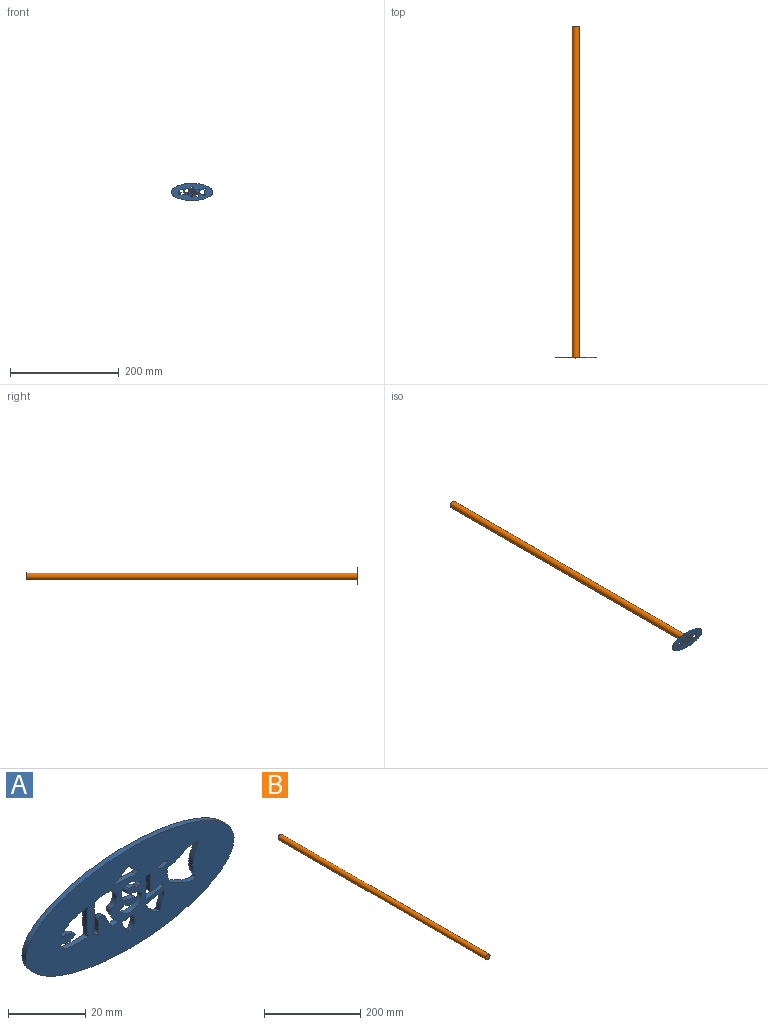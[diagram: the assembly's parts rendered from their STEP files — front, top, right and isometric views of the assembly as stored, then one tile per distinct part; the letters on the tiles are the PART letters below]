
ASSEMBLY  parts=2 mates=1
PART A: 74 faces, bbox 76.2x1.6x31.8 mm
  f0: plane 76.2x31.75mm, normal (0,-1,0), area 1556.4mm2, adj f2,f3,f4,f5,f6,f7,f8,f9
  f1: plane 76.2x31.75mm, normal (0,1,0), area 1556.4mm2, adj f2,f3,f4,f5,f6,f7,f8,f9
  f2: extruded ~76.2x31.75mm, area 280.8mm2, adj f0,f1
  f3: cylinder r=18.2mm len=1.77mm, axis (0,-1,0), area 2.9mm2, adj f0,f1,f4,f9
  f4: cylinder r=740.75mm len=7.68mm, axis (0,-1,0), area 12.2mm2, adj f0,f1,f3,f5
  f5: cylinder r=37.19mm len=6.75mm, axis (0,-1,0), area 10.9mm2, adj f0,f1,f4,f6
  f6: cylinder r=4.49mm len=1.59mm, axis (0,-1,0), area 1.1mm2, adj f0,f1,f5,f7
  f7: cylinder r=0.59mm len=1.59mm, axis (0,-1,0), area 1.5mm2, adj f0,f1,f6,f8
  f8: cylinder r=127.81mm len=3.97mm, axis (0,-1,0), area 6.4mm2, adj f0,f1,f7,f9
  f9: cylinder r=424.89mm len=5.64mm, axis (0,-1,0), area 9mm2, adj f0,f1,f3,f8
  f10: cylinder r=145.51mm len=6.76mm, axis (0,-1,0), area 11mm2, adj f0,f1,f11,f13
  f11: cylinder r=9.14mm len=5.32mm, axis (0,-1,0), area 11.6mm2, adj f0,f1,f10,f12
  f12: cylinder r=9.63mm len=3.56mm, axis (0,-1,0), area 6mm2, adj f0,f1,f11,f13
  f13: cylinder r=3.4mm len=2.63mm, axis (0,-1,0), area 4.3mm2, adj f0,f1,f10,f12
  f14: cylinder r=0.35mm len=1.59mm, axis (0,-1,0), area 1.1mm2, adj f0,f1,f15,f17
  f15: cylinder r=2.95mm len=3.55mm, axis (0,-1,0), area 6.2mm2, adj f0,f1,f14,f16
  f16: cylinder r=3.58mm len=1.59mm, axis (0,-1,0), area 2.4mm2, adj f0,f1,f15,f17
  f17: cylinder r=16.1mm len=2.17mm, axis (0,-1,0), area 3.6mm2, adj f0,f1,f14,f16
  f18: cylinder r=12.75mm len=5.47mm, axis (0,-1,0), area 9.2mm2, adj f0,f1,f19,f25
  f19: cylinder r=6.86mm len=5.43mm, axis (0,-1,0), area 9.1mm2, adj f0,f1,f18,f20
  f20: cylinder r=41.77mm len=4.82mm, axis (0,-1,0), area 8.4mm2, adj f0,f1,f19,f21
  f21: cylinder r=10.69mm len=4.41mm, axis (0,-1,0), area 7.3mm2, adj f0,f1,f20,f22
  f22: cylinder r=0.46mm len=1.59mm, axis (0,-1,0), area 1.4mm2, adj f0,f1,f21,f23
  f23: cylinder r=7.17mm len=7.4mm, axis (0,-1,0), area 12.4mm2, adj f0,f1,f22,f24
  f24: cylinder r=84.15mm len=3.6mm, axis (0,-1,0), area 6.3mm2, adj f0,f1,f23,f25
  f25: cylinder r=10.84mm len=6.23mm, axis (0,-1,0), area 10.2mm2, adj f0,f1,f18,f24
  f26: cylinder r=117.25mm len=9.33mm, axis (0,-1,0), area 14.8mm2, adj f0,f1,f27,f38
  f27: cylinder r=1.23mm len=1.59mm, axis (0,-1,0), area 2.5mm2, adj f0,f1,f26,f28
  f28: cylinder r=0.52mm len=1.59mm, axis (0,-1,0), area 1.5mm2, adj f0,f1,f27,f29
  f29: cylinder r=29.74mm len=3.77mm, axis (0,-1,0), area 6mm2, adj f0,f1,f28,f30
  f30: cylinder r=0.75mm len=1.59mm, axis (0,-1,0), area 1.7mm2, adj f0,f1,f29,f31
  f31: cylinder r=1.82mm len=1.68mm, axis (0,-1,0), area 3.3mm2, adj f0,f1,f30,f32
  f32: cylinder r=66.39mm len=4.18mm, axis (0,-1,0), area 7.6mm2, adj f0,f1,f31,f33
  f33: cylinder r=5.51mm len=2.03mm, axis (0,-1,0), area 3.4mm2, adj f0,f1,f32,f34
  f34: cylinder r=65.37mm len=4.03mm, axis (0,-1,0), area 7.5mm2, adj f0,f1,f33,f35
  f35: cylinder r=0.86mm len=1.59mm, axis (0,-1,0), area 2.2mm2, adj f0,f1,f34,f36
  f36: cylinder r=3.11mm len=5.81mm, axis (0,-1,0), area 12mm2, adj f0,f1,f35,f37
  f37: cylinder r=30.77mm len=4.91mm, axis (0,-1,0), area 7.8mm2, adj f0,f1,f36,f38
  f38: cylinder r=1.01mm len=1.59mm, axis (0,-1,0), area 2.2mm2, adj f0,f1,f26,f37
  f39: plane 4.74x3.32mm, normal (0.57,0,-0.82), area 9.2mm2, adj f0,f1,f40,f44
  f40: cylinder r=80.95mm len=8.03mm, axis (0,-1,0), area 12.8mm2, adj f0,f1,f39,f41
  f41: cylinder r=1.92mm len=1.59mm, axis (0,-1,0), area 1.7mm2, adj f0,f1,f40,f42
  f42: cylinder r=0.12mm len=1.59mm, axis (0,-1,0), area 0.4mm2, adj f0,f1,f41,f43
  f43: cylinder r=8.66mm len=3.16mm, axis (0,-1,0), area 6.9mm2, adj f0,f1,f42,f44
  f44: cylinder r=0.59mm len=1.59mm, axis (0,-1,0), area 1.8mm2, adj f0,f1,f39,f43
  f45: cylinder r=0.21mm len=1.59mm, axis (0,-1,0), area 0.5mm2, adj f0,f1,f46,f58
  f46: cylinder r=6.71mm len=5.36mm, axis (0,-1,0), area 9.3mm2, adj f0,f1,f45,f47
  f47: cylinder r=2.58mm len=5.05mm, axis (0,-1,0), area 11.4mm2, adj f0,f1,f46,f48
  f48: cylinder r=22.95mm len=2.74mm, axis (0,-1,0), area 4.4mm2, adj f0,f1,f47,f49
  f49: cylinder r=0.6mm len=1.59mm, axis (0,-1,0), area 2.1mm2, adj f0,f1,f48,f50
  f50: cylinder r=2.79mm len=3.95mm, axis (0,-1,0), area 7.1mm2, adj f0,f1,f49,f51
  f51: cylinder r=3.1mm len=1.8mm, axis (0,-1,0), area 3.4mm2, adj f0,f1,f50,f52
  f52: cylinder r=4.54mm len=7.99mm, axis (0,-1,0), area 15.6mm2, adj f0,f1,f51,f53
  f53: cylinder r=1.9mm len=2.34mm, axis (0,-1,0), area 4.6mm2, adj f0,f1,f52,f54
  f54: cylinder r=25.07mm len=3.7mm, axis (0,-1,0), area 6.1mm2, adj f0,f1,f53,f55
  f55: cylinder r=0.81mm len=1.59mm, axis (0,-1,0), area 3.6mm2, adj f0,f1,f54,f56
  f56: cylinder r=3.93mm len=2.81mm, axis (0,-1,0), area 4.8mm2, adj f0,f1,f55,f57
  f57: cylinder r=0.73mm len=1.59mm, axis (0,-1,0), area 1.2mm2, adj f0,f1,f56,f58
  f58: cylinder r=87.09mm len=1.59mm, axis (0,-1,0), area 1.5mm2, adj f0,f1,f45,f57
  f59: cylinder r=23.05mm len=3.68mm, axis (0,-1,0), area 5.9mm2, adj f0,f1,f60,f62
  f60: cylinder r=7.12mm len=4.49mm, axis (0,-1,0), area 9.1mm2, adj f0,f1,f59,f61
  f61: cylinder r=3.67mm len=3.03mm, axis (0,-1,0), area 5.6mm2, adj f0,f1,f60,f62
  f62: cylinder r=1.75mm len=1.85mm, axis (0,-1,0), area 3.7mm2, adj f0,f1,f59,f61
  f63: cylinder r=34.29mm len=9.52mm, axis (0,-1,0), area 15.2mm2, adj f0,f1,f64,f73
  f64: cylinder r=15.85mm len=9.45mm, axis (0,-1,0), area 16.4mm2, adj f0,f1,f63,f65
  f65: cylinder r=1.23mm len=1.59mm, axis (0,-1,0), area 2mm2, adj f0,f1,f64,f66
  f66: cylinder r=0.65mm len=1.59mm, axis (0,-1,0), area 1.5mm2, adj f0,f1,f65,f67
  f67: cylinder r=2.14mm len=1.59mm, axis (0,-1,0), area 2.2mm2, adj f0,f1,f66,f68
  f68: cylinder r=10.09mm len=3.16mm, axis (0,-1,0), area 5.6mm2, adj f0,f1,f67,f69
  f69: cylinder r=4.65mm len=3.5mm, axis (0,-1,0), area 6mm2, adj f0,f1,f68,f70
  f70: cylinder r=2.74mm len=1.59mm, axis (0,-1,0), area 2.4mm2, adj f0,f1,f69,f71
  f71: cylinder r=0.34mm len=1.59mm, axis (0,-1,0), area 1.4mm2, adj f0,f1,f70,f72
  f72: cylinder r=2.56mm len=1.88mm, axis (0,-1,0), area 4.3mm2, adj f0,f1,f71,f73
  f73: cylinder r=37.14mm len=8.24mm, axis (0,-1,0), area 13.1mm2, adj f0,f1,f63,f72
PART B: 3 faces, bbox 12.7x609.6x12.7 mm
  f0: cylinder r=6.35mm len=609.6mm, axis (0,1,0), area 24322mm2, adj f1,f2
  f1: plane 12.7x12.7mm, normal (0,-1,0), area 126.7mm2, adj f0
  f2: plane 12.7x12.7mm, normal (0,1,0), area 126.7mm2, adj f0
PLACE A t=(66.95,-289.55,79.99)mm
PLACE B t=(66.84,320.05,80)mm
MATE fastened A.f1 <-> B.f0  axis (0,1,0) through (66.84,-289.55,80)mm
